FCSTD DOCUMENT  (FreeCAD 1.0R39109 (Git))
Label: cubesat_laser_cut_parts
License: All rights reserved
LicenseURL: https://en.wikipedia.org/wiki/All_rights_reserved
objects: Sketcher::SketchObject×1, PartDesign::Body×1
note: 3 computed .brp shape members not serialized (recipe doc carries the construction recipe); baked Part::Feature solids carry a one-line shape summary decoded from their .brp

FEATURE [Sketcher::SketchObject] Sketch
  ArcFitTolerance = 1e-06
  AttachmentSupport = -> [XY_Plane]
  FullyConstrained = false
  MakeInternals = false
  MapMode = 5
  sketch-geometry (101):
    g0: LineSegment StartX=102.831 StartY=15.6253 StartZ=0 EndX=114.831 EndY=15.6253 EndZ=0
    g1: LineSegment StartX=114.831 StartY=67.6253 StartZ=0 EndX=102.831 EndY=67.6253 EndZ=0
    g2: LineSegment StartX=114.831 StartY=15.6253 StartZ=0 EndX=114.831 EndY=18.6253 EndZ=0
    g3: LineSegment StartX=114.831 StartY=18.6253 StartZ=0 EndX=124.831 EndY=18.6253 EndZ=0
    g4: LineSegment StartX=124.831 StartY=18.6253 StartZ=0 EndX=124.831 EndY=64.6253 EndZ=0
    g5: LineSegment StartX=124.831 StartY=64.6253 StartZ=0 EndX=114.831 EndY=64.6253 EndZ=0
    g6: LineSegment StartX=114.831 StartY=64.6253 StartZ=0 EndX=114.831 EndY=67.6253 EndZ=0
    g7: LineSegment StartX=102.831 StartY=67.6253 StartZ=0 EndX=102.831 EndY=64.6253 EndZ=0
    g8: LineSegment StartX=78.8315 StartY=67.6253 StartZ=0 EndX=78.8315 EndY=15.6253 EndZ=0
    g9: LineSegment StartX=102.831 StartY=15.6253 StartZ=0 EndX=102.831 EndY=18.6253 EndZ=0
    g10: LineSegment StartX=78.8315 StartY=93.1533 StartZ=0 EndX=81.8315 EndY=93.1533 EndZ=0
    g11: LineSegment StartX=81.8315 StartY=93.1533 StartZ=0 EndX=81.8315 EndY=80.1533 EndZ=0
    g12: LineSegment StartX=81.8315 StartY=80.1533 StartZ=0 EndX=102.831 EndY=80.1533 EndZ=0
    g13: LineSegment StartX=102.831 StartY=80.1533 StartZ=0 EndX=102.831 EndY=83.1533 EndZ=0
    g14: LineSegment StartX=102.831 StartY=83.1533 StartZ=0 EndX=114.831 EndY=83.1533 EndZ=0
    g15: LineSegment StartX=114.831 StartY=83.1533 StartZ=0 EndX=114.831 EndY=80.1533 EndZ=0
    g16: LineSegment StartX=114.831 StartY=80.1533 StartZ=0 EndX=124.831 EndY=80.1533 EndZ=0
    g17: LineSegment StartX=124.831 StartY=80.1533 StartZ=0 EndX=124.831 EndY=173.153 EndZ=0
    g18: LineSegment StartX=124.831 StartY=173.153 StartZ=0 EndX=114.831 EndY=173.153 EndZ=0
    g19: LineSegment StartX=114.831 StartY=173.153 StartZ=0 EndX=114.831 EndY=170.153 EndZ=0
    g20: LineSegment StartX=114.831 StartY=170.153 StartZ=0 EndX=102.831 EndY=170.153 EndZ=0
    g21: LineSegment StartX=102.831 StartY=170.153 StartZ=0 EndX=102.831 EndY=173.153 EndZ=0
    g22: LineSegment StartX=102.831 StartY=173.153 StartZ=0 EndX=81.8315 EndY=173.153 EndZ=0
    g23: LineSegment StartX=81.8315 StartY=173.153 StartZ=0 EndX=81.8315 EndY=160.153 EndZ=0
    g24: LineSegment StartX=81.8315 StartY=160.153 StartZ=0 EndX=78.8315 EndY=160.153 EndZ=0
    g25: LineSegment StartX=78.8315 StartY=160.153 StartZ=0 EndX=78.8315 EndY=93.1533 EndZ=0
    g26: LineSegment StartX=118.981 StartY=100.153 StartZ=0 EndX=118.981 EndY=90.1533 EndZ=0
    g27: LineSegment StartX=118.981 StartY=90.1533 StartZ=0 EndX=121.831 EndY=90.1533 EndZ=0
    g28: LineSegment StartX=121.831 StartY=90.1533 StartZ=0 EndX=121.831 EndY=100.153 EndZ=0
    g29: LineSegment StartX=121.831 StartY=100.153 StartZ=0 EndX=118.981 EndY=100.153 EndZ=0
    g30: LineSegment StartX=118.981 StartY=163.153 StartZ=0 EndX=118.981 EndY=153.153 EndZ=0
    g31: LineSegment StartX=118.981 StartY=153.153 StartZ=0 EndX=121.831 EndY=153.153 EndZ=0
    g32: LineSegment StartX=121.831 StartY=153.153 StartZ=0 EndX=121.831 EndY=163.153 EndZ=0
    g33: LineSegment StartX=121.831 StartY=163.153 StartZ=0 EndX=118.981 EndY=163.153 EndZ=0
    g34: LineSegment StartX=137.223 StartY=170.153 StartZ=0 EndX=137.223 EndY=163.153 EndZ=0
    g35: LineSegment StartX=137.223 StartY=163.153 StartZ=0 EndX=134.223 EndY=163.153 EndZ=0
    g36: LineSegment StartX=134.223 StartY=163.153 StartZ=0 EndX=134.223 EndY=153.153 EndZ=0
    g37: LineSegment StartX=134.223 StartY=153.153 StartZ=0 EndX=137.223 EndY=153.153 EndZ=0
    g38: LineSegment StartX=137.223 StartY=153.153 StartZ=0 EndX=137.223 EndY=104.153 EndZ=0
    g39: LineSegment StartX=183.223 StartY=83.1533 StartZ=0 EndX=183.223 EndY=90.1533 EndZ=0
    g40: LineSegment StartX=183.223 StartY=90.1533 StartZ=0 EndX=186.223 EndY=90.1533 EndZ=0
    g41: LineSegment StartX=186.223 StartY=90.1533 StartZ=0 EndX=186.223 EndY=100.153 EndZ=0
    g42: LineSegment StartX=186.223 StartY=100.153 StartZ=0 EndX=183.223 EndY=100.153 EndZ=0
    g43: LineSegment StartX=183.223 StartY=100.153 StartZ=0 EndX=183.223 EndY=153.153 EndZ=0
    g44: LineSegment StartX=183.223 StartY=153.153 StartZ=0 EndX=186.223 EndY=153.153 EndZ=0
    g45: LineSegment StartX=186.223 StartY=153.153 StartZ=0 EndX=186.223 EndY=163.153 EndZ=0
    g46: LineSegment StartX=186.223 StartY=163.153 StartZ=0 EndX=183.223 EndY=163.153 EndZ=0
    g47: LineSegment StartX=183.223 StartY=163.153 StartZ=0 EndX=183.223 EndY=170.153 EndZ=0
    g48: LineSegment StartX=183.223 StartY=170.153 StartZ=0 EndX=137.223 EndY=170.153 EndZ=0
    g49: LineSegment StartX=149.223 StartY=83.1533 StartZ=0 EndX=149.223 EndY=104.153 EndZ=0
    g50: LineSegment StartX=149.223 StartY=104.153 StartZ=0 EndX=137.223 EndY=104.153 EndZ=0
    g51: LineSegment StartX=183.223 StartY=83.1533 StartZ=0 EndX=149.223 EndY=83.1533 EndZ=0
    g52: LineSegment StartX=104.631 StartY=100.153 StartZ=0 EndX=104.631 EndY=90.1533 EndZ=0
    g53: LineSegment StartX=104.631 StartY=90.1533 StartZ=0 EndX=107.481 EndY=90.1533 EndZ=0
    g54: LineSegment StartX=107.481 StartY=90.1533 StartZ=0 EndX=107.481 EndY=100.153 EndZ=0
    g55: LineSegment StartX=107.481 StartY=100.153 StartZ=0 EndX=104.631 EndY=100.153 EndZ=0
    g56: LineSegment StartX=104.631 StartY=163.153 StartZ=0 EndX=104.631 EndY=153.153 EndZ=0
    g57: LineSegment StartX=104.631 StartY=153.153 StartZ=0 EndX=107.481 EndY=153.153 EndZ=0
    g58: LineSegment StartX=107.481 StartY=153.153 StartZ=0 EndX=107.481 EndY=163.153 EndZ=0
    g59: LineSegment StartX=107.481 StartY=163.153 StartZ=0 EndX=104.631 EndY=163.153 EndZ=0
    g60: LineSegment StartX=193.181 StartY=170.153 StartZ=0 EndX=193.181 EndY=163.153 EndZ=0
    g61: LineSegment StartX=193.181 StartY=163.153 StartZ=0 EndX=190.181 EndY=163.153 EndZ=0
    g62: LineSegment StartX=190.181 StartY=163.153 StartZ=0 EndX=190.181 EndY=153.153 EndZ=0
    g63: LineSegment StartX=190.181 StartY=153.153 StartZ=0 EndX=193.181 EndY=153.153 EndZ=0
    g64: LineSegment StartX=193.181 StartY=153.153 StartZ=0 EndX=193.181 EndY=126.653 EndZ=0
    g65: LineSegment StartX=239.181 StartY=83.1533 StartZ=0 EndX=239.181 EndY=90.1533 EndZ=0
    g66: LineSegment StartX=239.181 StartY=90.1533 StartZ=0 EndX=242.181 EndY=90.1533 EndZ=0
    g67: LineSegment StartX=242.181 StartY=90.1533 StartZ=0 EndX=242.181 EndY=100.153 EndZ=0
    g68: LineSegment StartX=242.181 StartY=100.153 StartZ=0 EndX=239.181 EndY=100.153 EndZ=0
    g69: LineSegment StartX=239.181 StartY=100.153 StartZ=0 EndX=239.181 EndY=153.153 EndZ=0
    g70: LineSegment StartX=239.181 StartY=153.153 StartZ=0 EndX=242.181 EndY=153.153 EndZ=0
    g71: LineSegment StartX=242.181 StartY=153.153 StartZ=0 EndX=242.181 EndY=163.153 EndZ=0
    g72: LineSegment StartX=242.181 StartY=163.153 StartZ=0 EndX=239.181 EndY=163.153 EndZ=0
    g73: LineSegment StartX=239.181 StartY=163.153 StartZ=0 EndX=239.181 EndY=170.153 EndZ=0
    g74: LineSegment StartX=239.181 StartY=170.153 StartZ=0 EndX=193.181 EndY=170.153 EndZ=0
    g75: LineSegment StartX=206.181 StartY=83.1533 StartZ=0 EndX=206.181 EndY=126.653 EndZ=0
    g76: LineSegment StartX=206.181 StartY=126.653 StartZ=0 EndX=193.181 EndY=126.653 EndZ=0
    g77: LineSegment StartX=239.181 StartY=83.1533 StartZ=0 EndX=206.181 EndY=83.1533 EndZ=0
    g78: LineSegment StartX=102.831 StartY=64.6253 StartZ=0 EndX=81.8315 EndY=64.6253 EndZ=0
    g79: LineSegment StartX=81.8315 StartY=64.6253 StartZ=0 EndX=81.8315 EndY=67.6253 EndZ=0
    g80: LineSegment StartX=81.8315 StartY=67.6253 StartZ=0 EndX=78.8315 EndY=67.6253 EndZ=0
    g81: LineSegment StartX=102.831 StartY=18.6253 StartZ=0 EndX=81.8315 EndY=18.6253 EndZ=0
    g82: LineSegment StartX=81.8315 StartY=18.6253 StartZ=0 EndX=81.8315 EndY=15.6253 EndZ=0
    g83: LineSegment StartX=81.8315 StartY=15.6253 StartZ=0 EndX=78.8315 EndY=15.6253 EndZ=0
    g84: LineSegment StartX=62.1701 StartY=170.153 StartZ=0 EndX=10.1701 EndY=170.153 EndZ=0
    g85: LineSegment StartX=62.1701 StartY=170.153 StartZ=0 EndX=62.1701 EndY=160.153 EndZ=0
    g86: LineSegment StartX=62.1701 StartY=160.153 StartZ=0 EndX=59.1701 EndY=160.153 EndZ=0
    g87: LineSegment StartX=59.1701 StartY=160.153 StartZ=0 EndX=59.1701 EndY=93.1533 EndZ=0
    g88: LineSegment StartX=59.1701 StartY=93.1533 StartZ=0 EndX=62.1701 EndY=93.1533 EndZ=0
    g89: LineSegment StartX=62.1701 StartY=93.1533 StartZ=0 EndX=62.1701 EndY=83.1533 EndZ=0
    g90: LineSegment StartX=62.1701 StartY=83.1533 StartZ=0 EndX=10.1701 EndY=83.1533 EndZ=0
    g91: LineSegment StartX=10.1701 StartY=83.1533 StartZ=0 EndX=10.1701 EndY=93.1533 EndZ=0
    g92: LineSegment StartX=10.1701 StartY=93.1533 StartZ=0 EndX=13.1701 EndY=93.1533 EndZ=0
    g93: LineSegment StartX=13.1701 StartY=93.1533 StartZ=0 EndX=13.1701 EndY=160.153 EndZ=0
    g94: LineSegment StartX=13.1701 StartY=160.153 StartZ=0 EndX=10.1701 EndY=160.153 EndZ=0
    g95: LineSegment StartX=10.1701 StartY=160.153 StartZ=0 EndX=10.1701 EndY=170.153 EndZ=0
    g96: Circle CenterX=235.181 CenterY=141.653 CenterZ=0 NormalX=0 NormalY=0 NormalZ=1 AngleXU=0 Radius=2
    g97: Circle CenterX=235.181 CenterY=124.653 CenterZ=0 NormalX=0 NormalY=0 NormalZ=1 AngleXU=0 Radius=2
    g98: Circle CenterX=235.181 CenterY=107.653 CenterZ=0 NormalX=0 NormalY=0 NormalZ=1 AngleXU=0 Radius=2
    g99: Circle CenterX=235.181 CenterY=90.6533 CenterZ=0 NormalX=0 NormalY=0 NormalZ=1 AngleXU=0 Radius=2
    g100: Circle CenterX=235.181 CenterY=158.653 CenterZ=0 NormalX=0 NormalY=0 NormalZ=1 AngleXU=0 Radius=2
  constraints (297):
    c: Horizontal(g0)
    c: Horizontal(g1)
    c: Coincident(g2,g0)
    c: Vertical(g2)
    c: Coincident(g3,g2)
    c: Horizontal(g3)
    c: Coincident(g4,g3)
    c: Vertical(g4)
    c: Coincident(g5,g4)
    c: Horizontal(g5)
    c: Coincident(g6,g5)
    c: Coincident(g6,g1)
    c: Vertical(g6)
    c: Coincident(g7,g1)
    c: Vertical(g7)
    c: Vertical(g8)
    c: Coincident(g9,g0)
    c: Vertical(g9)
    c: DistanceX(g8,g3) = 46
    c: DistanceY(g2,g2) = 3
    c: DistanceY(g9,g9) = 3
    c: DistanceY(g6,g6) = 3
    c: DistanceY(g7,g7) = 3
    c: DistanceX(g5,g2) = 0
    c: DistanceX(g7,g9) = 0
    c: DistanceX(g0,g0) = 12
    c: DistanceY(g0,g1) = 52
    c: Horizontal(g10)
    c: Coincident(g11,g10)
    c: Vertical(g11)
    c: Coincident(g12,g11)
    c: Horizontal(g12)
    c: Coincident(g13,g12)
    c: Vertical(g13)
    c: Coincident(g14,g13)
    c: Horizontal(g14)
    c: Coincident(g15,g14)
    c: Vertical(g15)
    c: Coincident(g16,g15)
    c: Horizontal(g16)
    c: Coincident(g17,g16)
    c: Vertical(g17)
    c: Coincident(g18,g17)
    c: Horizontal(g18)
    c: Coincident(g19,g18)
    c: Vertical(g19)
    c: Coincident(g20,g19)
    c: Horizontal(g20)
    c: Coincident(g21,g20)
    c: Vertical(g21)
    c: Coincident(g22,g21)
    c: Horizontal(g22)
    c: Coincident(g23,g22)
    c: Vertical(g23)
    c: Coincident(g24,g23)
    c: Horizontal(g24)
    c: Coincident(g25,g24)
    c: Coincident(g25,g10)
    c: Vertical(g25)
    c: DistanceY(g13,g13) = 3
    c: DistanceY(g15,g12) = 0
    c: DistanceY(g21,g21) = 3
    c: DistanceY(g18,g21) = 0
    c: DistanceY(g11,g11) = 13
    c: DistanceY(g23,g23) = 13
    c: DistanceY(g17,g17) = 93
    c: DistanceX(g14,g19) = 0
    c: DistanceX(g13,g20) = 0
    c: DistanceX(g10,g10) = 3
    c: DistanceX(g10,g23) = 0
    c: DistanceX(g4,g16) = 0
    c: DistanceX(g15,g1) = 0
    c: DistanceX(g12,g1) = 0
    c: DistanceX(g8,g10) = 0
    c: Coincident(g26,g27)
    c: Coincident(g27,g28)
    c: Coincident(g28,g29)
    c: Coincident(g29,g26)
    c: Vertical(g26)
    c: Vertical(g28)
    c: Horizontal(g27)
    c: Horizontal(g29)
    c: DistanceX(g29,g29) = 2.85
    c: DistanceY(g26,g26) = 10
    c: Coincident(g30,g31)
    c: Coincident(g31,g32)
    c: Coincident(g32,g33)
    c: Coincident(g33,g30)
    c: Vertical(g30)
    c: Vertical(g32)
    c: Horizontal(g31)
    c: Horizontal(g33)
    c: DistanceX(g33,g33) = 2.85
    c: DistanceY(g30,g30) = 10
    c: DistanceX(g27,g16) = 3
    c: DistanceX(g28,g31) = 0
    c: DistanceY(g32,g17) = 10
    c: Vertical(g34)
    c: Coincident(g35,g34)
    c: Horizontal(g35)
    c: Coincident(g36,g35)
    c: Vertical(g36)
    c: Coincident(g37,g36)
    c: Horizontal(g37)
    c: Coincident(g38,g37)
    c: Vertical(g38)
    c: Vertical(g39)
    c: Coincident(g40,g39)
    c: Horizontal(g40)
    c: Coincident(g41,g40)
    c: Vertical(g41)
    c: Coincident(g42,g41)
    c: Horizontal(g42)
    c: Coincident(g43,g42)
    c: Vertical(g43)
    c: Coincident(g44,g43)
    c: Horizontal(g44)
    c: Coincident(g45,g44)
    c: Vertical(g45)
    c: Coincident(g46,g45)
    c: Horizontal(g46)
    c: Coincident(g47,g46)
    c: Vertical(g47)
    c: Coincident(g48,g47)
    c: Coincident(g48,g34)
    c: Horizontal(g48)
    c: DistanceX(g35,g35) = 3
    c: DistanceX(g37,g34) = 0
    c: DistanceX(g46,g46) = 3
    c: DistanceX(g43,g46) = 0
    c: DistanceX(g42,g42) = 3
    c: DistanceX(g42,g39) = 0
    c: DistanceY(g35,g32) = 0
    c: DistanceY(g31,g36) = 0
    c: DistanceY(g19,g34) = 0
    c: DistanceY(g46,g34) = 0
    c: DistanceY(g43,g37) = 0
    c: DistanceY(g16,g27) = 10
    c: Coincident(g49,g50)
    c: Vertical(g49)
    c: Horizontal(g50)
    c: Coincident(g51,g39)
    c: Coincident(g51,g49)
    c: Horizontal(g51)
    c: DistanceX(g50,g50) = 12
    c: DistanceX(g48,g48) = 46
    c: Coincident(g52,g53)
    c: Coincident(g53,g54)
    c: Coincident(g54,g55)
    c: Coincident(g55,g52)
    c: Vertical(g52)
    c: Vertical(g54)
    c: Horizontal(g53)
    c: Horizontal(g55)
    c: DistanceX(g55,g55) = 2.85
    c: DistanceY(g52,g52) = 10
    c: Coincident(g56,g57)
    c: Coincident(g57,g58)
    c: Coincident(g58,g59)
    c: Coincident(g59,g56)
    c: Vertical(g56)
    c: Vertical(g58)
    c: Horizontal(g57)
    c: Horizontal(g59)
    c: DistanceX(g59,g59) = 2.85
    c: DistanceY(g56,g56) = 10
    c: DistanceX(g54,g57) = 0
    c: DistanceY(g58,g30) = 0
    c: DistanceY(g26,g54) = 0
    c: Vertical(g60)
    c: Coincident(g61,g60)
    c: Horizontal(g61)
    c: Coincident(g62,g61)
    c: Vertical(g62)
    c: Coincident(g63,g62)
    c: Horizontal(g63)
    c: Coincident(g64,g63)
    c: Vertical(g64)
    c: Vertical(g65)
    c: Coincident(g66,g65)
    c: Horizontal(g66)
    c: Coincident(g67,g66)
    c: Vertical(g67)
    c: Coincident(g68,g67)
    c: Horizontal(g68)
    c: Coincident(g69,g68)
    c: Vertical(g69)
    c: Coincident(g70,g69)
    c: Horizontal(g70)
    c: Coincident(g71,g70)
    c: Vertical(g71)
    c: Coincident(g72,g71)
    c: Horizontal(g72)
    c: Coincident(g73,g72)
    c: Vertical(g73)
    c: Coincident(g74,g73)
    c: Coincident(g74,g60)
    c: Horizontal(g74)
    c: DistanceX(g61,g61) = 3
    c: DistanceX(g63,g60) = 0
    c: DistanceX(g72,g72) = 3
    c: DistanceX(g69,g72) = 0
    c: DistanceX(g68,g68) = 3
    c: DistanceX(g68,g65) = 0
    c: DistanceY(g72,g60) = 0
    c: DistanceY(g69,g63) = 0
    c: Coincident(g75,g76)
    c: Vertical(g75)
    c: Horizontal(g76)
    c: Coincident(g77,g65)
    c: Coincident(g77,g75)
    c: Horizontal(g77)
    c: DistanceX(g76,g76) = 13
    c: DistanceX(g74,g74) = 46
    c: DistanceY(g61,g45) = 0
    c: DistanceY(g62,g62) = 10
    c: DistanceY(g47,g60) = 0
    c: DistanceY(g75,g39) = 0
    c: Coincident(g76,g64)
    c: DistanceY(g75,g75) = 43.5
    c: DistanceY(g41,g68) = 0
    c: Coincident(g50,g38)
    c: DistanceY(g49,g14) = 0
    c: DistanceY(g28,g42) = 0
    c: DistanceY(g49,g49) = 21
    c: DistanceY(g41,g41) = 10
    c: DistanceY(g67,g67) = 10
    c: DistanceX(g57,g30) = 11.5
    c: Coincident(g78,g7)
    c: Horizontal(g78)
    c: Coincident(g79,g78)
    c: Vertical(g79)
    c: Coincident(g80,g79)
    c: Horizontal(g80)
    c: Coincident(g8,g80)
    c: DistanceY(g79,g79) = 3
    c: DistanceX(g80,g80) = 3
    c: Coincident(g81,g9)
    c: Horizontal(g81)
    c: Coincident(g82,g81)
    c: Vertical(g82)
    c: Coincident(g83,g82)
    c: Horizontal(g83)
    c: Coincident(g8,g83)
    c: DistanceY(g82,g82) = 3
    c: DistanceX(g83,g83) = 3
    c: DistanceX(g3,g3) = 10
    c: Horizontal(g84)
    c: Coincident(g85,g84)
    c: Vertical(g85)
    c: Coincident(g86,g85)
    c: Horizontal(g86)
    c: Coincident(g87,g86)
    c: Vertical(g87)
    c: Coincident(g88,g87)
    c: Horizontal(g88)
    c: Coincident(g89,g88)
    c: Vertical(g89)
    c: Coincident(g90,g89)
    c: Horizontal(g90)
    c: Coincident(g91,g90)
    c: Vertical(g91)
    c: Coincident(g92,g91)
    c: Horizontal(g92)
    c: Coincident(g93,g92)
    c: Vertical(g93)
    c: Coincident(g94,g93)
    c: Horizontal(g94)
    c: Coincident(g95,g94)
    c: Coincident(g95,g84)
    c: Vertical(g95)
    c: DistanceY(g93,g86) = 0
    c: DistanceY(g92,g87) = 0
    c: DistanceX(g92,g92) = 3
    c: DistanceX(g94,g94) = 3
    c: DistanceX(g86,g86) = 3
    c: DistanceX(g88,g88) = 3
    c: DistanceY(g85,g85) = 10
    c: DistanceY(g89,g89) = 10
    c: DistanceY(g20,g84) = 0
    c: DistanceY(g89,g13) = 0
    c: DistanceX(g84,g84) = 52
    c: Diameter(g96) = 4
    c: Diameter(g97) = 4
    c: Diameter(g98) = 4
    c: Diameter(g99) = 4
    c: Diameter(g100) = 4
    c: DistanceX(g99,g65) = 4
    c: DistanceX(g98,g99) = 0
    c: DistanceX(g97,g99) = 0
    c: DistanceX(g96,g99) = 0
    c: DistanceX(g100,g99) = 0
    c: DistanceY(g65,g99) = 7.5
    c: DistanceY(g99,g98) = 17
    c: DistanceY(g98,g97) = 17
    c: DistanceY(g97,g96) = 17
    c: DistanceY(g96,g100) = 17
FEATURE [PartDesign::Body] Body
  AllowCompound = false
  Group = -> [Sketch]
  Origin = -> Origin
